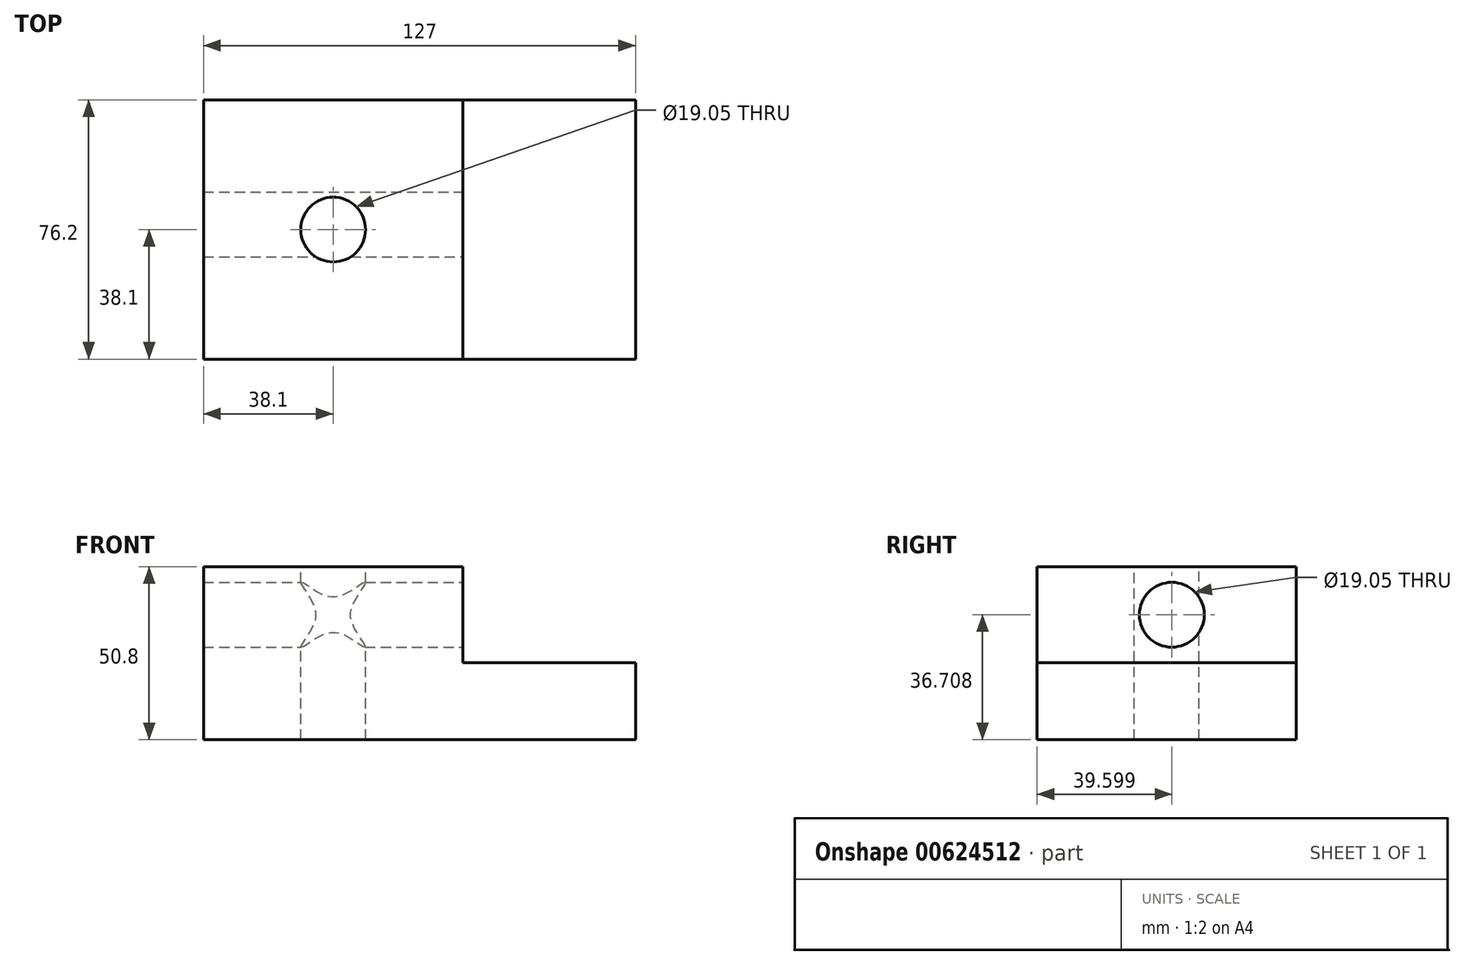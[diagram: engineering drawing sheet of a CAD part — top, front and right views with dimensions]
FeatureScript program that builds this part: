
annotation { "Feature Type Name" : "Feature", "Feature Type Description" : "" }
export const myFeature = defineFeature(function(context is Context, id is Id, definition is map)
    precondition{}
    {
        {
            var Q0;
            Q0=qCreatedBy(makeId("Front.planeOp"),FACE);
            var sketch = newSketch(context, id + "F0", { "sketchPlane" : qUnion([Q0])});
            skLineSegment(sketch, "E0.bottom", {"start": v(-127, -75.23) * mm, "end": v(0, -75.23) * mm});
            skLineSegment(sketch, "E0.top", {"start": v(-127, -126.03) * mm, "end": v(0, -126.03) * mm});
            skLineSegment(sketch, "E0.left", {"start": v(-127, -75.23) * mm, "end": v(-127, -126.03) * mm});
            skLineSegment(sketch, "E0.right", {"start": v(0, -75.23) * mm, "end": v(0, -126.03) * mm});
            skLineSegment(sketch, "E1", {"start": v(0, -103.41) * mm, "end": v(-50.8, -103.41) * mm});
            skLineSegment(sketch, "E2", {"start": v(-50.8, -75.23) * mm, "end": v(-50.8, -103.41) * mm});
            skSolve(sketch);
        }
        {
            var Q0;
            {var subQ1=sQuery(id+"F0.wireOp",EDGE,"E0.top");Q0=makeQuery(id+"F0.imprint","IMPRINT",FACE,{"disambiguationData":[TD([[makeQuery(id+"F0.imprint","IMPRINT",EDGE,{"derivedFrom":subQ1}),1.0]])]});}
            extrude(context, id + "F1", {"entities" : qUnion([Q0]), "depth" : 76.2 * mm, "offsetDistance" : 25.4 * mm});
        }
        {
            var Q0;
            Q0=makeQuery(id+"F1.opExtrude","SWEPT_FACE",FACE,{"disambiguationData":[OSD([sQuery(id+"F0.wireOp",EDGE,"E2")])]});
            var sketch = newSketch(context, id + "F2", { "sketchPlane" : qUnion([Q0])});
            skPoint(sketch, "E3", {"position": v(0, -89.32) * mm});
            skPoint(sketch, "E4", {"position": v(-38.1, -75.23) * mm});
            skPoint(sketch, "E5", {"position": v(-36.6, -89.32) * mm});
            skSolve(sketch);
        }
        {
            var Q0;
            Q0=sQuery(id+"F2.wireOp",VERTEX,"E5");
            var Q1;
            Q1=makeQuery(id+"F1.opExtrude","SWEPT_BODY",BODY,{"disambiguationData":[OSD([sQuery(id+"F0.wireOp",EDGE,"E0.bottom"),sQuery(id+"F0.wireOp",EDGE,"E0.top"),sQuery(id+"F0.wireOp",EDGE,"E0.left"),sQuery(id+"F0.wireOp",EDGE,"E0.right"),sQuery(id+"F0.wireOp",EDGE,"E1"),sQuery(id+"F0.wireOp",EDGE,"E2")])]});
            hole(context, id + "F3", {"style" : HoleStyle.SIMPLE, "endStyle" : HoleEndStyle.THROUGH, "holeDiameter" : 19.05 * mm, "majorDiameter" : 6.35 * mm, "isTappedThrough" : true, "tappedDepth" : 12.7 * mm, "tapClearance" : 3, "locations" : qUnion([Q0]), "scope" : qUnion([Q1])});
        }
        {
            var Q0;
            Q0=makeQuery(id+"F1.opExtrude","SWEPT_FACE",FACE,{"disambiguationData":[OSD([sQuery(id+"F0.wireOp",EDGE,"E0.bottom")])]});
            var sketch = newSketch(context, id + "F4", { "sketchPlane" : qUnion([Q0])});
            skPoint(sketch, "E6", {"position": v(-50.8, -38.1) * mm});
            skPoint(sketch, "E7", {"position": v(-88.9, 0) * mm});
            skPoint(sketch, "E8", {"position": v(-88.9, -38.1) * mm});
            skSolve(sketch);
        }
        {
            var Q0;
            Q0=sQuery(id+"F4.wireOp",VERTEX,"E8");
            var Q1;
            Q1=makeQuery(id+"F1.opExtrude","SWEPT_BODY",BODY,{"disambiguationData":[OSD([sQuery(id+"F0.wireOp",EDGE,"E0.bottom"),sQuery(id+"F0.wireOp",EDGE,"E0.top"),sQuery(id+"F0.wireOp",EDGE,"E0.left"),sQuery(id+"F0.wireOp",EDGE,"E0.right"),sQuery(id+"F0.wireOp",EDGE,"E1"),sQuery(id+"F0.wireOp",EDGE,"E2")])]});
            hole(context, id + "F5", {"style" : HoleStyle.SIMPLE, "endStyle" : HoleEndStyle.THROUGH, "holeDiameter" : 19.05 * mm, "majorDiameter" : 6.35 * mm, "isTappedThrough" : true, "tappedDepth" : 12.7 * mm, "tapClearance" : 3, "locations" : qUnion([Q0]), "scope" : qUnion([Q1])});
        }
    });
